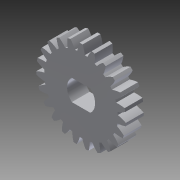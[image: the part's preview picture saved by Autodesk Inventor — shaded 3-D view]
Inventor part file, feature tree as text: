
AUTODESK INVENTOR PART (.ipt)
format: ipt  version: 2013 (Build 170138000, 138)  size: 257,536 bytes
history: native  units: mm (DEFAULTED — no unit token found)
features: plane x3, other x3, sketch x3, extrude x2
ambient origin geometry x8: Origin, YZ Plane, XZ Plane, XY Plane, X Axis, Y Axis, Z Axis, Center Point
bodies: Solid1 (feature_tree)
feature tree (11):
  extrude  "Extrusion1"  Depth=6.35mm TaperAngle=0.0deg
  plane  "Work Plane1"
  plane  "Work Plane2"
  plane  "Work Plane3"
  other  "Spur Gear"
  extrude  "Extrusion2"  Depth=76.2mm TaperAngle=0.0deg
  sketch  "Sketch1"  dims[d0=31.90875mm d1=6.35mm d2=0.0mm]
  sketch  "Sketch2"  dims[d3=29.21mm d4=76.2mm d5=0.0mm]
  other  "Srf1"
  sketch  "Sketch3"  dims[d6=0.0mm d7=1.36591mm d9=0.0mm d14=0.0mm d15=304.8mm d16=0.0mm d17=0.0mm d18=0.0mm d19=304.8mm d20=25.4mm d21=0.0mm]
  other  "Pitch Diameter"
